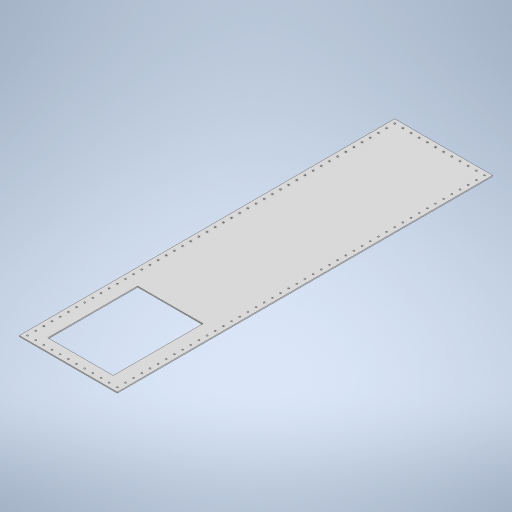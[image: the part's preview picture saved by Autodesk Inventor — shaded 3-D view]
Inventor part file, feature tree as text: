
AUTODESK INVENTOR PART (.ipt)
format: ipt  version: 2023.4 (Build 274418000, 418)  size: 418,816 bytes
history: native  units: in
note: dims shown in document units (in); Inventor stores cm internally (conversion verified against a paired STEP export)
features: sheet_metal_op x1, extrude x1, other x1, sketch x1
ambient origin geometry x8: Origin, YZ Plane, XZ Plane, XY Plane, X Axis, Y Axis, Z Axis, Center Point
bodies: Body1 (feature_tree)
feature tree (4):
  sheet_metal_op  "Face2"
  extrude  "Extrusion6"  Depth=12.0in
  other  "Plate2"
  sketch  "Sketch4"  dims[d0=46.0in d1=12.0in d3=0.197in d4=0.5in d5=0.5in d6=0.197in d7=0.5in d8=0.5in d9=4.7244in d11=1.0in d12=0.3937in d14=1.0in d16=18.1102in d18=1.0in d19=0.3937in d21=1.0in d23=4.7244in d25=1.0in d26=0.3937in d28=1.0in d30=17.7165in d32=1.0in d33=0.3937in d35=1.0in d37=0.125in d83=8.0in d84=11.0in d85=2.0in d86=2.0in d87=1.5in d88=1.0in d89=0.0in d49=0.5in d50=0.0344in d51=0.5in d52=0.0344in]
